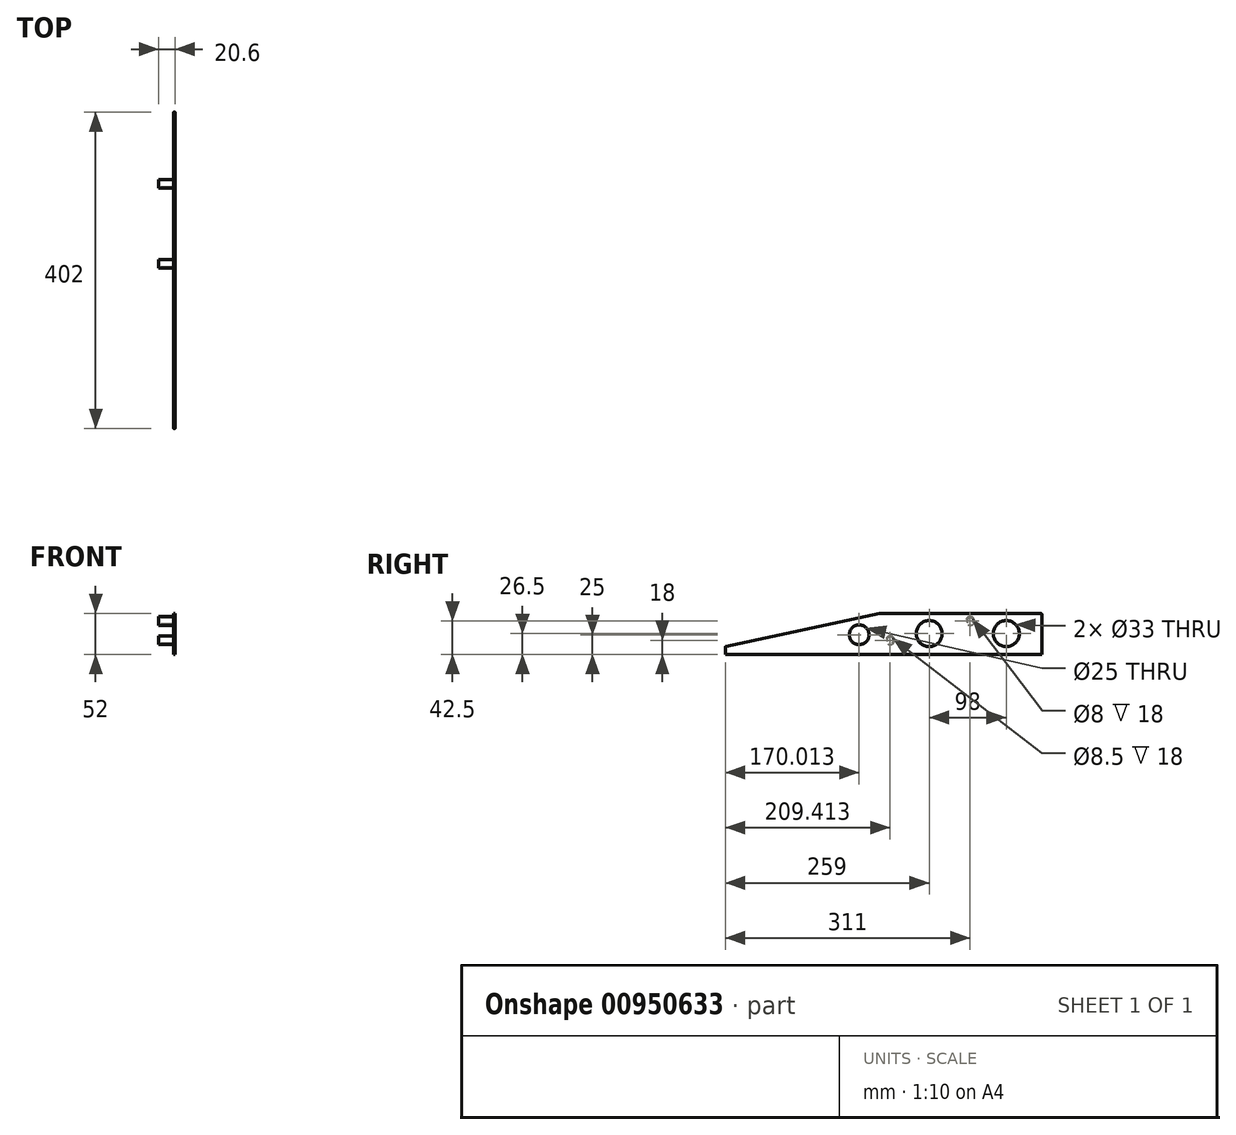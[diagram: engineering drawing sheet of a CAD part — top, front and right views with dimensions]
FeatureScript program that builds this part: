
annotation { "Feature Type Name" : "Feature", "Feature Type Description" : "" }
export const myFeature = defineFeature(function(context is Context, id is Id, definition is map)
    precondition{}
    {
        {
            var Q0;
            Q0=qCreatedBy(makeId("Right.planeOp"),FACE);
            var sketch = newSketch(context, id + "F0", { "sketchPlane" : qUnion([Q0])});
            skLineSegment(sketch, "E0.bottom", {"start": v(0, 0) * mm, "end": v(-402, 0) * mm});
            skLineSegment(sketch, "E0.top", {"start": v(-1, 52) * mm, "end": v(-206, 52) * mm});
            skLineSegment(sketch, "E0.left", {"start": v(0, 0) * mm, "end": v(0, 51) * mm});
            skLineSegment(sketch, "E0.right", {"start": v(-402, 0) * mm, "end": v(-402, 9.2) * mm});
            skLineSegment(sketch, "E1", {"start": v(-206, 125.72) * mm, "end": v(-206, -128.19) * mm, "construction": true});
            skLineSegment(sketch, "E2", {"start": v(-419.17, 10) * mm, "end": v(-375.98, 10) * mm, "construction": true});
            skLineSegment(sketch, "E3", {"start": v(-401.2, 10.17) * mm, "end": v(-206, 52) * mm});
            skCircle(sketch, "E4", {"center": v(-45, 26.5) * mm, "radius": 16.5 * mm});
            skCircle(sketch, "E5", {"center": v(-143, 26.5) * mm, "radius": 16.5 * mm});
            skCircle(sketch, "E6", {"center": v(-231.99, 25) * mm, "radius": 12.5 * mm});
            skPoint(sketch, "E7.visualSharp", {"position": v(0, 52) * mm});
            skArc(sketch, "E7.filletArc", {"start": v(0, 51) * mm, "mid": v(-0.3, 51.7) * mm, "end": v(-1, 52) * mm});
            skPoint(sketch, "E8.visualSharp", {"position": v(-402, 10) * mm});
            skArc(sketch, "E8.filletArc", {"start": v(-401.2, 10.17) * mm, "mid": v(-401.78, 9.82) * mm, "end": v(-402, 9.2) * mm});
            skLineSegment(sketch, "E9", {"start": v(-91, 101.03) * mm, "end": v(-91, -36.09) * mm, "construction": true});
            skLineSegment(sketch, "E10", {"start": v(-79.68, 42.5) * mm, "end": v(-106.78, 42.5) * mm, "construction": true});
            skCircle(sketch, "E11", {"center": v(-91, 42.5) * mm, "radius": 5.5 * mm});
            skLineSegment(sketch, "E12", {"start": v(-171.4, 18) * mm, "end": v(-217.23, 18) * mm, "construction": true});
            skLineSegment(sketch, "E13", {"start": v(-192.59, 34) * mm, "end": v(-192.59, -20.85) * mm, "construction": true});
            skCircle(sketch, "E14", {"center": v(-192.59, 18) * mm, "radius": 5.5 * mm});
            skCircle(sketch, "E15", {"center": v(-91, 42.5) * mm, "radius": 4.25 * mm});
            skCircle(sketch, "E16", {"center": v(-192.59, 18) * mm, "radius": 4.25 * mm});
            skSolve(sketch);
        }
        {
            var Q0;
            Q0 = qSketchRegion(id + "F0", true);
            extrude(context, id + "F1", {"entities" : qUnion([Q0]), "depth" : 1.6 * mm, "offsetDistance" : 25 * mm});
        }
        {
            var Q0;
            Q0=makeQuery(id+"F0.imprint","IMPRINT",FACE,{"disambiguationData":[TD([[makeQuery(id+"F0.imprint","IMPRINT",EDGE,{"derivedFrom":sQuery(id+"F0.wireOp",EDGE,"E11")}),1.0]])]});
            var Q1;
            Q1=makeQuery(id+"F0.imprint","IMPRINT",FACE,{"disambiguationData":[TD([[makeQuery(id+"F0.imprint","IMPRINT",EDGE,{"derivedFrom":sQuery(id+"F0.wireOp",EDGE,"E15")}),1.0]])]});
            var Q2;
            Q2=makeQuery(id+"F0.imprint","IMPRINT",FACE,{"disambiguationData":[TD([[makeQuery(id+"F0.imprint","IMPRINT",EDGE,{"derivedFrom":sQuery(id+"F0.wireOp",EDGE,"E16")}),1.0]])]});
            var Q3;
            Q3=makeQuery(id+"F0.imprint","IMPRINT",FACE,{"disambiguationData":[TD([[makeQuery(id+"F0.imprint","IMPRINT",EDGE,{"derivedFrom":sQuery(id+"F0.wireOp",EDGE,"E14")}),1.0]])]});
            extrude(context, id + "F2", {"entities" : qUnion([Q0, Q1, Q2, Q3]), "operationType" : NewBodyOperationType.ADD, "oppositeDirection" : true, "depth" : 19 * mm, "offsetDistance" : 25 * mm, "hasSecondDirection" : true, "secondDirectionOppositeDirection" : false, "secondDirectionDepth" : 1.6 * mm});
        }
        {
            var Q0;
            Q0=makeQuery(id+"F2.opExtrude","CAP_FACE",FACE,{"disambiguationData":[OSD([sQuery(id+"F0.wireOp",EDGE,"E11")])],"isStart":false});
            var sketch = newSketch(context, id + "F3", { "sketchPlane" : qUnion([Q0])});
            skCircle(sketch, "E17", {"center": v(91, 42.5) * mm, "radius": 4 * mm});
            skSolve(sketch);
        }
        {
            var Q0;
            Q0=makeQuery(id+"F3.imprint","IMPRINT",FACE,{"disambiguationData":[TD([[makeQuery(id+"F3.imprint","IMPRINT",EDGE,{"derivedFrom":sQuery(id+"F3.wireOp",EDGE,"E17")}),1.0]])]});
            extrude(context, id + "F4", {"entities" : qUnion([Q0]), "operationType" : NewBodyOperationType.REMOVE, "oppositeDirection" : true, "depth" : 18 * mm, "offsetDistance" : 25 * mm});
        }
        {
            var Q0;
            Q0=makeQuery(id+"F2.opExtrude","CAP_FACE",FACE,{"disambiguationData":[OSD([sQuery(id+"F0.wireOp",EDGE,"E14")])],"isStart":false});
            var sketch = newSketch(context, id + "F5", { "sketchPlane" : qUnion([Q0])});
            skCircle(sketch, "E18", {"center": v(192.59, 18) * mm, "radius": 4.25 * mm});
            skSolve(sketch);
        }
        {
            var Q0;
            Q0=makeQuery(id+"F5.imprint","IMPRINT",FACE,{"disambiguationData":[TD([[makeQuery(id+"F5.imprint","IMPRINT",EDGE,{"derivedFrom":sQuery(id+"F5.wireOp",EDGE,"E18")}),1.0]])]});
            extrude(context, id + "F6", {"entities" : qUnion([Q0]), "operationType" : NewBodyOperationType.REMOVE, "oppositeDirection" : true, "depth" : 18 * mm, "offsetDistance" : 25 * mm});
        }
    });
